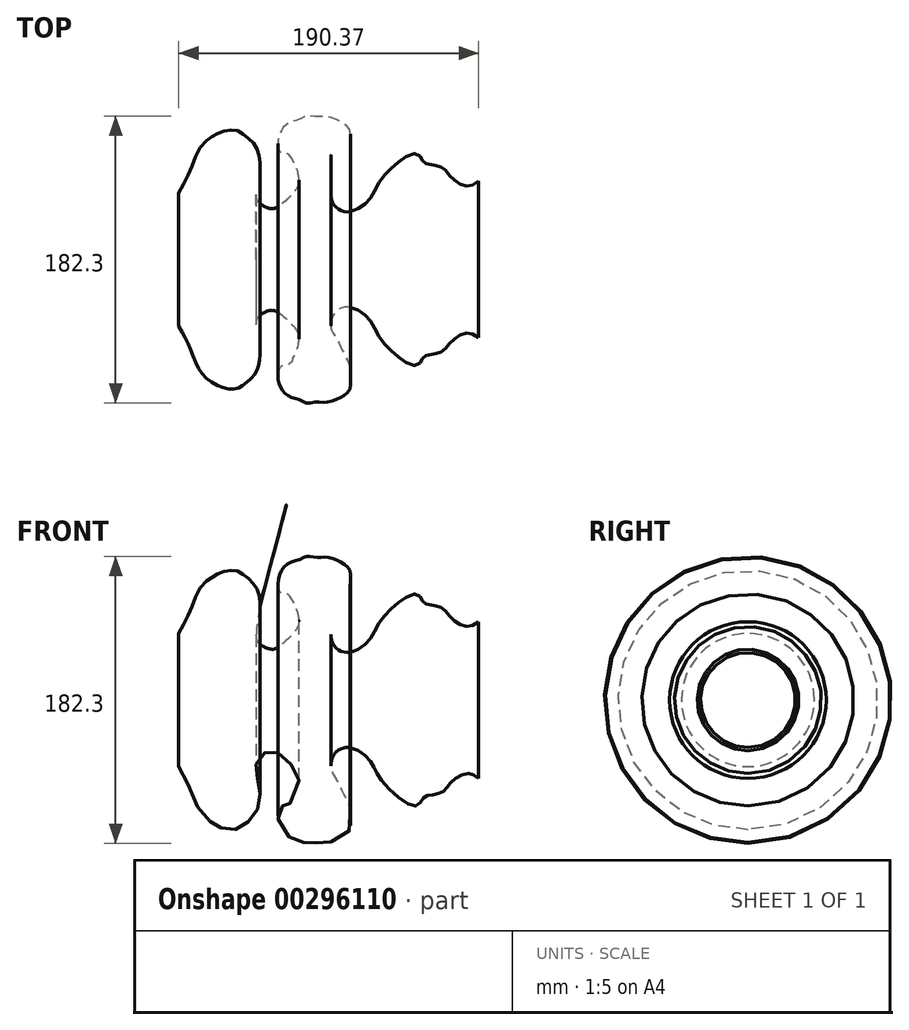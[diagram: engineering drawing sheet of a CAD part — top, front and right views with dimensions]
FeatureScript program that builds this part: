
annotation { "Feature Type Name" : "Feature", "Feature Type Description" : "" }
export const myFeature = defineFeature(function(context is Context, id is Id, definition is map)
    precondition{}
    {
        {
            var Q0;
            Q0=qCreatedBy(makeId("Front.planeOp"),FACE);
            var sketch = newSketch(context, id + "F0", { "sketchPlane" : qUnion([Q0])});
            skFitSpline(sketch, "E0", {"points": [v(-115.46, -25.11) * mm, v(-108.89, -12.25) * mm, v(-100.48, 5.52) * mm, v(-93.17, 11.29) * mm, v(-88.42, 13.75) * mm, v(-80.39, 14.98) * mm, v(-76.37, 13.58) * mm, v(-67.96, 6.5) * mm, v(-64.67, 0) * mm, v(-63.94, -8.78) * mm, v(-65.4, -16.87) * mm, v(-66.14, -24.02) * mm, v(-65.04, -30.65) * mm, v(-57.37, -35.01) * mm, v(-52.62, -34) * mm, v(-43.85, -26.36) * mm, v(-39.1, -15.85) * mm, v(-46.4, 0) * mm, v(-48.23, 0) * mm, v(-49.7, 0) * mm, v(-52.25, 4.1) * mm, v(-47.87, 17.79) * mm, v(-37.27, 22.3) * mm, v(-35.08, 23.67) * mm, v(-27.77, 23.22) * mm, v(-20.46, 23.14) * mm, v(-7.3, 15.98) * mm, v(-6.58, 8.15) * mm, v(-6.94, 0) * mm, v(-9.5, -5.48) * mm, v(-11.7, -10.14) * mm, v(-16.44, -19.18) * mm, v(-18.63, -23.47) * mm, v(-18.27, -29.57) * mm, v(-14.62, -35.1) * mm, v(-5.48, -36.84) * mm, v(6.94, -27.4) * mm, v(13.15, -16.48) * mm, v(35.08, 0) * mm, v(40.2, -5.39) * mm, v(46.4, -7.25) * mm, v(52.98, -9.73) * mm, v(57.73, -15.3) * mm, v(67.96, -20.76) * mm, v(74.9, -17.66) * mm], "startDerivative": vector(223.18, 393.67) * mm, "endDerivative": vector(293.94, 222.45) * mm});
            skLineSegment(sketch, "E1", {"start": v(-88.42, -67.36) * mm, "end": v(21.92, -67.36) * mm});
            skSolve(sketch);
        }
        {
            var Q0;
            Q0=sQuery(id+"F0.wireOp",EDGE,"E0");
            var Q1;
            Q1=sQuery(id+"F0.wireOp",EDGE,"E1");
            revolve(context, id + "F1", {"bodyType" : ToolBodyType.SURFACE, "surfaceEntities" : qUnion([Q0]), "axis" : qUnion([Q1]), "revolveType" : RevolveType.FULL});
        }
    });
